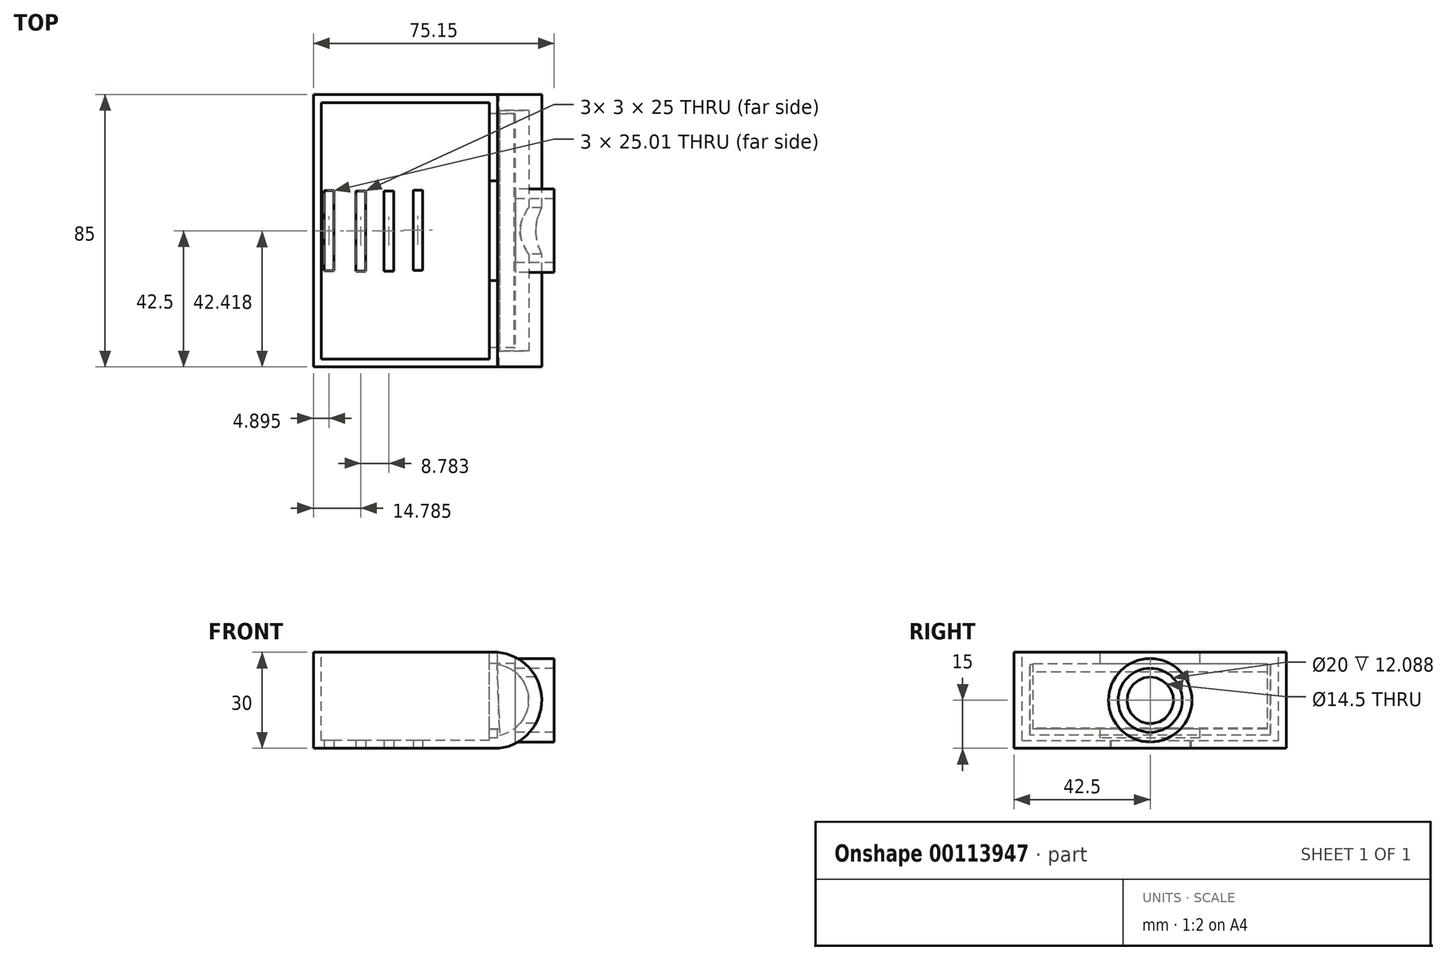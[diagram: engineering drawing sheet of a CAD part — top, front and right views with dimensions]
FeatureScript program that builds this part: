
annotation { "Feature Type Name" : "Feature", "Feature Type Description" : "" }
export const myFeature = defineFeature(function(context is Context, id is Id, definition is map)
    precondition{}
    {
        {
            var Q0;
            Q0=qCreatedBy(makeId("Front.planeOp"),FACE);
            var sketch = newSketch(context, id + "F0", { "sketchPlane" : qUnion([Q0])});
            skLineSegment(sketch, "E0.bottom", {"start": v(25.47, -15) * mm, "end": v(-32.5, -15) * mm});
            skLineSegment(sketch, "E0.top", {"start": v(24.94, 15) * mm, "end": v(-32.5, 15) * mm});
            skLineSegment(sketch, "E0.right", {"start": v(-32.5, -15) * mm, "end": v(-32.5, 15) * mm});
            skPoint(sketch, "E0.middle", {"position": v(0, 0) * mm});
            skArc(sketch, "E1", {"start": v(25.47, -15) * mm, "mid": v(38.67, 1.51) * mm, "end": v(22.4, 15) * mm});
            skPoint(sketch, "E2.orphan", {"position": v(32.5, 15) * mm});
            skPoint(sketch, "E3.orphan", {"position": v(32.5, -15) * mm});
            skLineSegment(sketch, "E4", {"start": v(25.01, 10.97) * mm, "end": v(25.4, -10.97) * mm});
            skArc(sketch, "E5.0", {"start": v(25, -11.03) * mm, "mid": v(34.75, -0.04) * mm, "end": v(25.01, 10.97) * mm});
            skSolve(sketch);
        }
        {
            var Q0;
            {var subQ6=sQuery(id+"F0.wireOp",EDGE,"E0.bottom");Q0=makeQuery(id+"F0.imprint","IMPRINT",FACE,{"disambiguationData":[TD([[makeQuery(id+"F0.imprint","IMPRINT",EDGE,{"derivedFrom":subQ6}),-1.0]])]});}
            var Q1;
            {var subQ0=sQuery(id+"F0.wireOp",EDGE,"E5.0");var subQ1=sQuery(id+"F0.wireOp",EDGE,"E4");var subQ2=makeQuery(id+"F0.imprint","INTERSECT",VERTEX,{"disambiguationData":[OD(0.0)],"derivedFrom":[subQ1,subQ0]});Q1=makeQuery(id+"F0.imprint","IMPRINT",FACE,{"disambiguationData":[TD([[makeQuery(id+"F0.imprint","IMPRINT",EDGE,{"disambiguationData":[TD([[subQ2,-1.0]])],"derivedFrom":subQ1}),1.0]])]});}
            var Q2;
            {var subQ0=sQuery(id+"F0.wireOp",EDGE,"E4");var subQ4=sQuery(id+"F0.wireOp",EDGE,"E5.0");var subQ5=makeQuery(id+"F0.imprint","INTERSECT",VERTEX,{"disambiguationData":[OD(0.0)],"derivedFrom":[subQ0,subQ4]});Q2=makeQuery(id+"F0.imprint","IMPRINT",FACE,{"disambiguationData":[TD([[makeQuery(id+"F0.imprint","IMPRINT",EDGE,{"disambiguationData":[TD([[subQ5,1.0]])],"derivedFrom":subQ4}),-1.0]])]});}
            extrude(context, id + "F1", {"entities" : qUnion([Q0, Q1, Q2]), "endBound" : BoundingType.SYMMETRIC, "depth" : 85 * mm});
        }
        {
            var Q0;
            Q0=qCreatedBy(makeId("Right.planeOp"),FACE);
            var sketch = newSketch(context, id + "F2", { "sketchPlane" : qUnion([Q0])});
            skCircle(sketch, "E6", {"center": v(0, 0) * mm, "radius": 7.25 * mm});
            skSolve(sketch);
        }
        {
            var Q0;
            Q0=makeQuery(id+"F2.imprint","IMPRINT",FACE,{"disambiguationData":[TD([[makeQuery(id+"F2.imprint","IMPRINT",EDGE,{"derivedFrom":sQuery(id+"F2.wireOp",EDGE,"E6")}),1.0]])]});
            extrude(context, id + "F3", {"entities" : qUnion([Q0]), "operationType" : NewBodyOperationType.REMOVE, "endBound" : BoundingType.THROUGH_ALL, "depth" : 40 * mm});
        }
        {
            var Q0;
            Q0=makeQuery(id+"F1.opExtrude","SWEPT_FACE",FACE,{"disambiguationData":[OSD([sQuery(id+"F0.wireOp",EDGE,"E0.bottom")])]});
            var sketch = newSketch(context, id + "F4", { "sketchPlane" : qUnion([Q0])});
            skLineSegment(sketch, "E7.bottom", {"start": v(-26.1, 12.5) * mm, "end": v(-29.1, 12.5) * mm});
            skLineSegment(sketch, "E7.top", {"start": v(-26.1, -12.5) * mm, "end": v(-29.1, -12.5) * mm});
            skLineSegment(sketch, "E7.left", {"start": v(-26.1, 12.5) * mm, "end": v(-26.1, -12.5) * mm});
            skLineSegment(sketch, "E7.right", {"start": v(-29.1, 12.5) * mm, "end": v(-29.1, -12.5) * mm});
            skPoint(sketch, "E7.middle", {"position": v(-27.6, 0) * mm});
            skLineSegment(sketch, "E8.bottom", {"start": v(-16.22, 12.58) * mm, "end": v(-19.21, 12.58) * mm});
            skLineSegment(sketch, "E8.top", {"start": v(-16.22, -12.42) * mm, "end": v(-19.21, -12.42) * mm});
            skLineSegment(sketch, "E8.left", {"start": v(-16.22, 12.58) * mm, "end": v(-16.22, -12.42) * mm});
            skLineSegment(sketch, "E8.right", {"start": v(-19.21, 12.58) * mm, "end": v(-19.21, -12.42) * mm});
            skPoint(sketch, "E8.middle", {"position": v(-17.72, 0.08) * mm});
            skLineSegment(sketch, "E9.bottom", {"start": v(-7.43, 12.58) * mm, "end": v(-10.43, 12.58) * mm});
            skLineSegment(sketch, "E9.top", {"start": v(-7.43, -12.42) * mm, "end": v(-10.43, -12.42) * mm});
            skLineSegment(sketch, "E9.left", {"start": v(-7.43, 12.58) * mm, "end": v(-7.43, -12.42) * mm});
            skLineSegment(sketch, "E9.right", {"start": v(-10.43, 12.58) * mm, "end": v(-10.43, -12.42) * mm});
            skPoint(sketch, "E9.middle", {"position": v(-8.93, 0.08) * mm});
            skLineSegment(sketch, "E10.bottom", {"start": v(1.63, 12.3) * mm, "end": v(-1.37, 12.3) * mm});
            skLineSegment(sketch, "E10.top", {"start": v(1.63, -12.7) * mm, "end": v(-1.37, -12.7) * mm});
            skLineSegment(sketch, "E10.left", {"start": v(1.63, 12.3) * mm, "end": v(1.63, -12.7) * mm});
            skLineSegment(sketch, "E10.right", {"start": v(-1.37, 12.3) * mm, "end": v(-1.37, -12.7) * mm});
            skPoint(sketch, "E10.middle", {"position": v(0.13, -0.2) * mm});
            skLineSegment(sketch, "E11", {"start": v(0, -42.5) * mm, "end": v(0, 42.5) * mm, "construction": true});
            skLineSegment(sketch, "E12.MirrorCS", {"start": v(7.43, -12.42) * mm, "end": v(10.43, -12.42) * mm});
            skPoint(sketch, "E13.MirrorP", {"position": v(8.93, 0.08) * mm});
            skLineSegment(sketch, "E14.MirrorCS", {"start": v(10.43, 12.58) * mm, "end": v(10.43, -12.42) * mm});
            skLineSegment(sketch, "E15.MirrorCS", {"start": v(7.43, 12.58) * mm, "end": v(7.43, -12.42) * mm});
            skLineSegment(sketch, "E16.MirrorCS", {"start": v(7.43, 12.58) * mm, "end": v(10.43, 12.58) * mm});
            skPoint(sketch, "E17.MirrorP", {"position": v(17.72, 0.08) * mm});
            skLineSegment(sketch, "E18.MirrorCS", {"start": v(16.22, 12.58) * mm, "end": v(19.21, 12.58) * mm});
            skLineSegment(sketch, "E19.MirrorCS", {"start": v(16.22, -12.42) * mm, "end": v(19.21, -12.42) * mm});
            skLineSegment(sketch, "E20.MirrorCS", {"start": v(16.22, 12.58) * mm, "end": v(16.22, -12.42) * mm});
            skLineSegment(sketch, "E21.MirrorCS", {"start": v(19.21, 12.58) * mm, "end": v(19.21, -12.42) * mm});
            skSolve(sketch);
        }
        {
            var Q0;
            Q0=makeQuery(id+"F4.imprint","IMPRINT",FACE,{"disambiguationData":[TD([[makeQuery(id+"F4.imprint","IMPRINT",EDGE,{"derivedFrom":sQuery(id+"F4.wireOp",EDGE,"E7.bottom")}),1.0]])]});
            var Q1;
            Q1=makeQuery(id+"F4.imprint","IMPRINT",FACE,{"disambiguationData":[TD([[makeQuery(id+"F4.imprint","IMPRINT",EDGE,{"derivedFrom":sQuery(id+"F4.wireOp",EDGE,"E8.bottom")}),1.0]])]});
            var Q2;
            Q2=makeQuery(id+"F4.imprint","IMPRINT",FACE,{"disambiguationData":[TD([[makeQuery(id+"F4.imprint","IMPRINT",EDGE,{"derivedFrom":sQuery(id+"F4.wireOp",EDGE,"E9.bottom")}),1.0]])]});
            var Q3;
            Q3=makeQuery(id+"F4.imprint","IMPRINT",FACE,{"disambiguationData":[TD([[makeQuery(id+"F4.imprint","IMPRINT",EDGE,{"derivedFrom":sQuery(id+"F4.wireOp",EDGE,"E10.bottom")}),1.0]])]});
            var Q4;
            Q4=makeQuery(id+"F4.imprint","IMPRINT",FACE,{"disambiguationData":[TD([[makeQuery(id+"F4.imprint","IMPRINT",EDGE,{"derivedFrom":sQuery(id+"F4.wireOp",EDGE,"05d96c94-c7e5-48ba-b86c-30f42af9bc471.MirrorCS")}),-1.0]])]});
            var Q5;
            Q5=makeQuery(id+"F4.imprint","IMPRINT",FACE,{"disambiguationData":[TD([[makeQuery(id+"F4.imprint","IMPRINT",EDGE,{"derivedFrom":sQuery(id+"F4.wireOp",EDGE,"fdd38d80-1933-40ed-8533-a17ed176e8e50.MirrorCS")}),1.0]])]});
            extrude(context, id + "F5", {"entities" : qUnion([Q0, Q1, Q2, Q3, Q4, Q5]), "operationType" : NewBodyOperationType.REMOVE, "endBound" : BoundingType.THROUGH_ALL, "oppositeDirection" : true, "depth" : 25 * mm});
        }
        {
            var Q0;
            Q0=makeQuery(id+"F1.opExtrude","SWEPT_FACE",FACE,{"disambiguationData":[OSD([sQuery(id+"F0.wireOp",EDGE,"E0.right")])]});
            var sketch = newSketch(context, id + "F6", { "sketchPlane" : qUnion([Q0])});
            skCircle(sketch, "E22", {"center": v(0, 11) * mm, "radius": 3 * mm});
            skSolve(sketch);
        }
        {
            var Q0;
            Q0=makeQuery(id+"F1.opExtrude","SWEPT_FACE",FACE,{"disambiguationData":[OSD([sQuery(id+"F0.wireOp",EDGE,"E0.top")])]});
            var sketch = newSketch(context, id + "F7", { "sketchPlane" : qUnion([Q0])});
            skLineSegment(sketch, "E23.0", {"start": v(22.44, 40) * mm, "end": v(-30, 40) * mm});
            skLineSegment(sketch, "E23.1", {"start": v(22.44, -40) * mm, "end": v(22.44, 40) * mm});
            skLineSegment(sketch, "E23.2", {"start": v(-30, -40) * mm, "end": v(22.44, -40) * mm});
            skLineSegment(sketch, "E23.3", {"start": v(-30, 40) * mm, "end": v(-30, -40) * mm});
            skSolve(sketch);
        }
        {
            var Q0;
            {var subQ2=sQuery(id+"F7.wireOp",EDGE,"E23.0");Q0=makeQuery(id+"F7.imprint","IMPRINT",FACE,{"disambiguationData":[TD([[makeQuery(id+"F7.imprint","IMPRINT",EDGE,{"derivedFrom":subQ2}),1.0]])]});}
            extrude(context, id + "F8", {"entities" : qUnion([Q0]), "operationType" : NewBodyOperationType.REMOVE, "oppositeDirection" : true, "depth" : 27.5 * mm});
        }
        {
            var Q0;
            Q0=qCreatedBy(makeId("Front.planeOp"),FACE);
            var sketch = newSketch(context, id + "F9", { "sketchPlane" : qUnion([Q0])});
            skArc(sketch, "E24", {"start": v(25.62, -10.87) * mm, "mid": v(34.67, 0.45) * mm, "end": v(24.83, 11.08) * mm});
            skLineSegment(sketch, "E25", {"start": v(24.83, 11.08) * mm, "end": v(25.62, -10.87) * mm});
            skSolve(sketch);
        }
        {
            var Q0;
            Q0 = qSketchRegion(id + "F9", true);
            extrude(context, id + "F10", {"entities" : qUnion([Q0]), "operationType" : NewBodyOperationType.REMOVE, "endBound" : BoundingType.SYMMETRIC, "oppositeDirection" : true, "depth" : 75 * mm});
        }
        {
            var Q0;
            Q0=makeQuery(id+"F8.boolean.opBoolean","COPY",FACE,{"derivedFrom":makeQuery(id+"F8.opExtrude","SWEPT_FACE",FACE,{"disambiguationData":[OSD([sQuery(id+"F7.wireOp",EDGE,"E23.1")])]})});
            var sketch = newSketch(context, id + "F11", { "sketchPlane" : qUnion([Q0])});
            skLineSegment(sketch, "E26.0", {"start": v(36.5, 11.5) * mm, "end": v(-36.5, 11.5) * mm});
            skLineSegment(sketch, "E26.1", {"start": v(36.5, -9) * mm, "end": v(36.5, 11.5) * mm});
            skLineSegment(sketch, "E26.2", {"start": v(-36.5, -9) * mm, "end": v(36.5, -9) * mm});
            skLineSegment(sketch, "E26.3", {"start": v(-36.5, 11.5) * mm, "end": v(-36.5, -9) * mm});
            skSolve(sketch);
        }
        {
            var Q0;
            Q0 = qSketchRegion(id + "F11", true);
            extrude(context, id + "F12", {"entities" : qUnion([Q0]), "operationType" : NewBodyOperationType.REMOVE, "oppositeDirection" : true, "depth" : 8 * mm});
        }
        {
            var Q0;
            Q0=makeQuery(id+"F1.opExtrude","SWEPT_FACE",FACE,{"disambiguationData":[OSD([sQuery(id+"F0.wireOp",EDGE,"E0.top")])]});
            var sketch = newSketch(context, id + "F13", { "sketchPlane" : qUnion([Q0])});
            skLineSegment(sketch, "E27.bottom", {"start": v(24.94, 15.55) * mm, "end": v(22.34, 15.55) * mm});
            skLineSegment(sketch, "E27.top", {"start": v(24.94, -15.55) * mm, "end": v(22.34, -15.55) * mm});
            skLineSegment(sketch, "E27.left", {"start": v(24.94, 15.55) * mm, "end": v(24.94, -15.55) * mm});
            skLineSegment(sketch, "E27.right", {"start": v(22.34, 15.55) * mm, "end": v(22.34, -15.55) * mm});
            skPoint(sketch, "E27.middle", {"position": v(23.64, 0) * mm});
            skPoint(sketch, "E27.middle.positionSnap0", {"position": v(24.94, 0) * mm});
            skPoint(sketch, "E27.centerSnap0", {"position": v(24.94, 0) * mm});
            skSolve(sketch);
        }
        {
            var Q0;
            Q0 = qSketchRegion(id + "F13", true);
            extrude(context, id + "F14", {"entities" : qUnion([Q0]), "operationType" : NewBodyOperationType.REMOVE, "oppositeDirection" : true, "depth" : 26.82 * mm});
        }
        {
            var Q0;
            Q0=makeQuery(id+"F8.boolean.opBoolean","COPY",FACE,{"derivedFrom":makeQuery(id+"F8.opExtrude","SWEPT_FACE",FACE,{"disambiguationData":[OSD([sQuery(id+"F7.wireOp",EDGE,"E23.3")])]})});
            var sketch = newSketch(context, id + "F15", { "sketchPlane" : qUnion([Q0])});
            skCircle(sketch, "E28", {"center": v(0, 0) * mm, "radius": 10 * mm});
            skCircle(sketch, "E29.0", {"center": v(0, 0) * mm, "radius": 13 * mm});
            skSolve(sketch);
        }
        {
            var Q0;
            Q0 = qSketchRegion(id + "F15", true);
            extrude(context, id + "F16", {"entities" : qUnion([Q0]), "depth" : 72.65 * mm, "hasSecondDirection" : true, "secondDirectionOppositeDirection" : false, "secondDirectionDepth" : 60.56 * mm});
        }
    });
